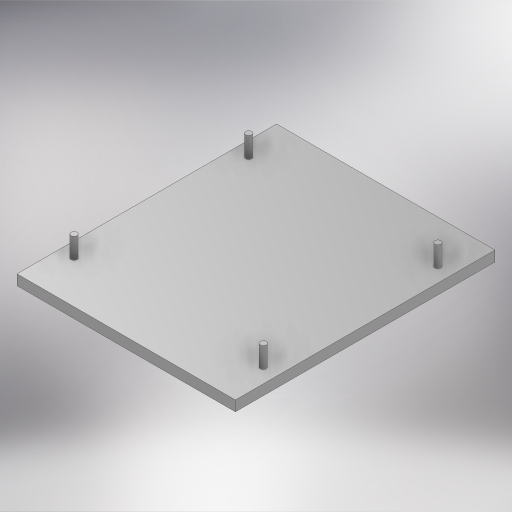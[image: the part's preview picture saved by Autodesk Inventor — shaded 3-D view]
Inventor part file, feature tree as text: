
AUTODESK INVENTOR PART (.ipt)
format: ipt  version: 2024 (Build 280153000, 153)  size: 339,456 bytes
history: native  units: mm
features: other x11, extrude x3, sketch x3
ambient origin geometry x8: Origin, YZ Plane, XZ Plane, XY Plane, X Axis, Y Axis, Z Axis, Center Point
bodies: Body1 (feature_tree)
feature tree (17):
  other  "Sólido1"
  extrude  "Extrusión1"  Depth=126.0mm
  extrude  "Extrusión2"  Depth=63.0mm
  extrude  "Extrusión3"  Depth=3.0mm
  sketch  "Boceto1"  dims[d1=106.0mm d2=126.0mm]
  sketch  "Boceto2"  dims[d3=53.0mm d4=63.0mm]
  sketch  "Boceto3"  dims[d5=5.0mm d6=0.0mm d7=3.0mm d8=20.616mm d9=7.071mm d10=10.0mm d11=0.0mm d12=52.5mm d13=126.0mm d14=106.0mm d15=52.5mm d16=35.0mm d17=35.0mm d18=35.0mm d19=35.0mm d20=35.0mm d21=2.0mm d22=0.0mm]
  other  "Finish1"
  other  "Finish2"
  other  "Finish3"
  other  "Finish4"
  other  "Finish5"
  other  "Finish6"
  other  "Finish7"
  other  "Finish8"
  other  "Finish9"
  other  "Finish10"
